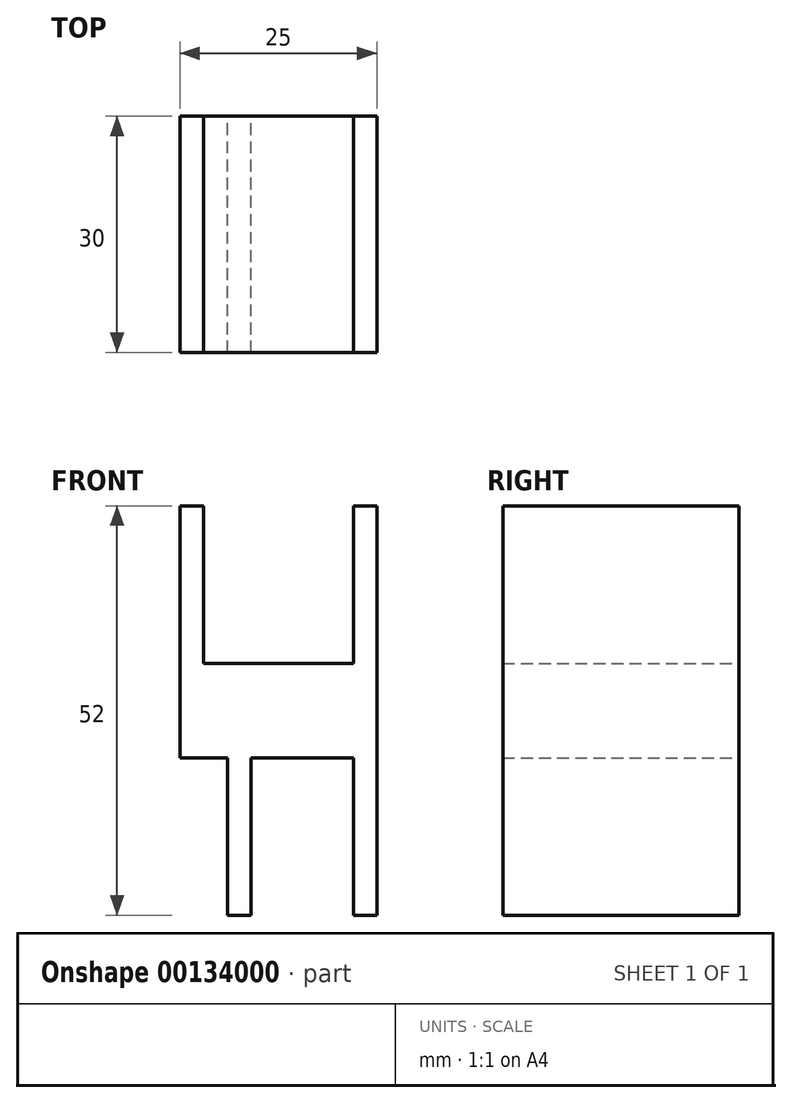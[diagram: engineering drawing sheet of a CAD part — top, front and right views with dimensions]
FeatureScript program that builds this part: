
annotation { "Feature Type Name" : "Feature", "Feature Type Description" : "" }
export const myFeature = defineFeature(function(context is Context, id is Id, definition is map)
    precondition{}
    {
        {
            var Q0;
            Q0=qCreatedBy(makeId("Front.planeOp"),FACE);
            var sketch = newSketch(context, id + "F0", { "sketchPlane" : qUnion([Q0])});
            skLineSegment(sketch, "E0.bottom", {"start": v(0, 0) * mm, "end": v(-19, 0) * mm});
            skLineSegment(sketch, "E0.left", {"start": v(0, 0) * mm, "end": v(0, 97.53) * mm});
            skLineSegment(sketch, "E0.right", {"start": v(-19, 0) * mm, "end": v(-19, 97.53) * mm});
            skLineSegment(sketch, "E1.bottom", {"start": v(0, 0) * mm, "end": v(-13, 0) * mm});
            skLineSegment(sketch, "E1.left", {"start": v(0, -12) * mm, "end": v(0, -32) * mm});
            skLineSegment(sketch, "E1.right", {"start": v(-13, -12) * mm, "end": v(-13, -29.3) * mm});
            skLineSegment(sketch, "E2.bottom", {"start": v(0, -32) * mm, "end": v(3, -32) * mm});
            skLineSegment(sketch, "E2.top", {"start": v(0, 20) * mm, "end": v(3, 20) * mm});
            skLineSegment(sketch, "E2.left", {"start": v(0, -32) * mm, "end": v(0, -12) * mm});
            skLineSegment(sketch, "E2.right", {"start": v(3, -32) * mm, "end": v(3, 20) * mm});
            skPoint(sketch, "E3", {"position": v(3, 0) * mm});
            skLineSegment(sketch, "E4.top", {"start": v(0, -12) * mm, "end": v(-13, -12) * mm});
            skLineSegment(sketch, "E5.bottom", {"start": v(-13, 0) * mm, "end": v(-16, 0) * mm});
            skLineSegment(sketch, "E5.top", {"start": v(-13, -32) * mm, "end": v(-16, -32) * mm});
            skLineSegment(sketch, "E5.left", {"start": v(-13, -12) * mm, "end": v(-13, -32) * mm});
            skLineSegment(sketch, "E5.right", {"start": v(-16, -12) * mm, "end": v(-16, -32) * mm});
            skLineSegment(sketch, "E6.top", {"start": v(-19, 20) * mm, "end": v(-22, 20) * mm});
            skLineSegment(sketch, "E6.left", {"start": v(-19, 0) * mm, "end": v(-19, 20) * mm});
            skLineSegment(sketch, "E6.right", {"start": v(-22, 0) * mm, "end": v(-22, 20) * mm});
            skLineSegment(sketch, "E7", {"start": v(-22, 0) * mm, "end": v(-22, -12) * mm});
            skLineSegment(sketch, "E8.trimOffspring", {"start": v(-16, -12) * mm, "end": v(-22, -12) * mm});
            skLineSegment(sketch, "E9.trimOffspring", {"start": v(0, 0) * mm, "end": v(0, 20) * mm});
            skSolve(sketch);
        }
        {
            var Q0;
            Q0 = qSketchRegion(id + "F0", true);
            extrude(context, id + "F1", {"entities" : qUnion([Q0]), "depth" : 15 * mm, "hasSecondDirection" : true, "secondDirectionOppositeDirection" : true, "secondDirectionDepth" : 15 * mm});
        }
    });
